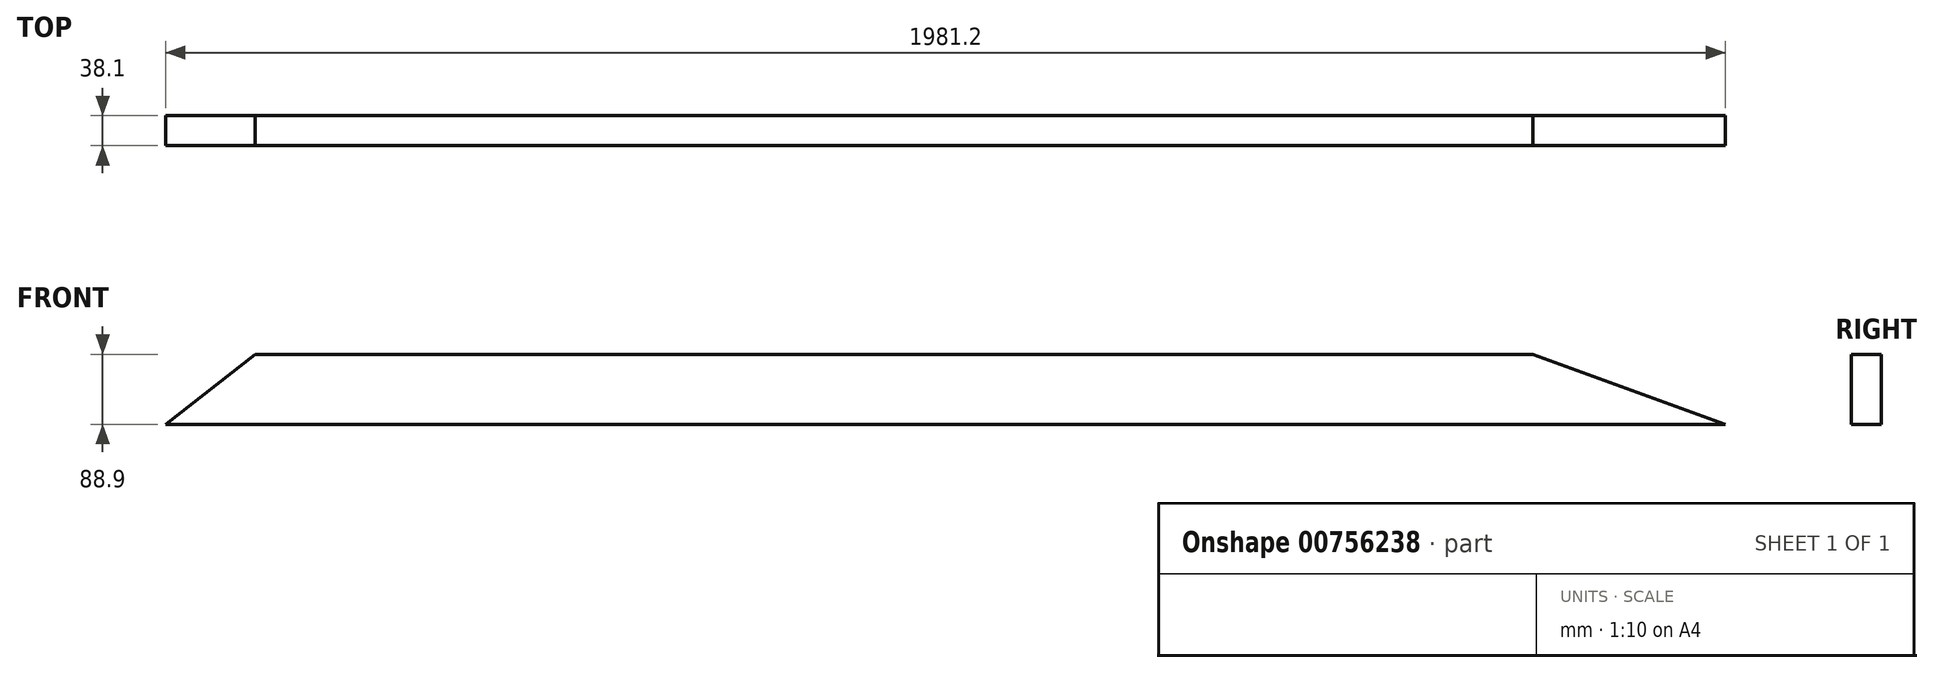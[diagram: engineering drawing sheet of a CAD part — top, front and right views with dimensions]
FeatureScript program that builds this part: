
annotation { "Feature Type Name" : "Feature", "Feature Type Description" : "" }
export const myFeature = defineFeature(function(context is Context, id is Id, definition is map)
    precondition{}
    {
        {
            var Q0;
            Q0=qCreatedBy(makeId("Front.planeOp"),FACE);
            var sketch = newSketch(context, id + "F0", { "sketchPlane" : qUnion([Q0])});
            skLineSegment(sketch, "E0.bottom", {"start": v(-990.6, -44.45) * mm, "end": v(990.6, -44.45) * mm});
            skLineSegment(sketch, "E0.top", {"start": v(-990.6, 44.45) * mm, "end": v(990.6, 44.45) * mm});
            skLineSegment(sketch, "E0.left", {"start": v(-990.6, -44.45) * mm, "end": v(-990.6, 44.45) * mm});
            skLineSegment(sketch, "E0.right", {"start": v(990.6, -44.45) * mm, "end": v(990.6, 44.45) * mm});
            skPoint(sketch, "E0.middle", {"position": v(0, 0) * mm});
            skLineSegment(sketch, "E1", {"start": v(990.6, -44.45) * mm, "end": v(746.35, 44.45) * mm});
            skLineSegment(sketch, "E2", {"start": v(-990.6, -44.45) * mm, "end": v(-876.81, 44.45) * mm});
            skSolve(sketch);
        }
        {
            var Q0;
            Q0=makeQuery(id+"F0.imprint","IMPRINT",FACE,{"disambiguationData":[TD([[makeQuery(id+"F0.imprint","IMPRINT",EDGE,{"derivedFrom":sQuery(id+"F0.wireOp",EDGE,"E0.bottom")}),1.0]])]});
            extrude(context, id + "F1", {"entities" : qUnion([Q0]), "depth" : 38.1 * mm, "offsetDistance" : 25.4 * mm});
        }
    });
